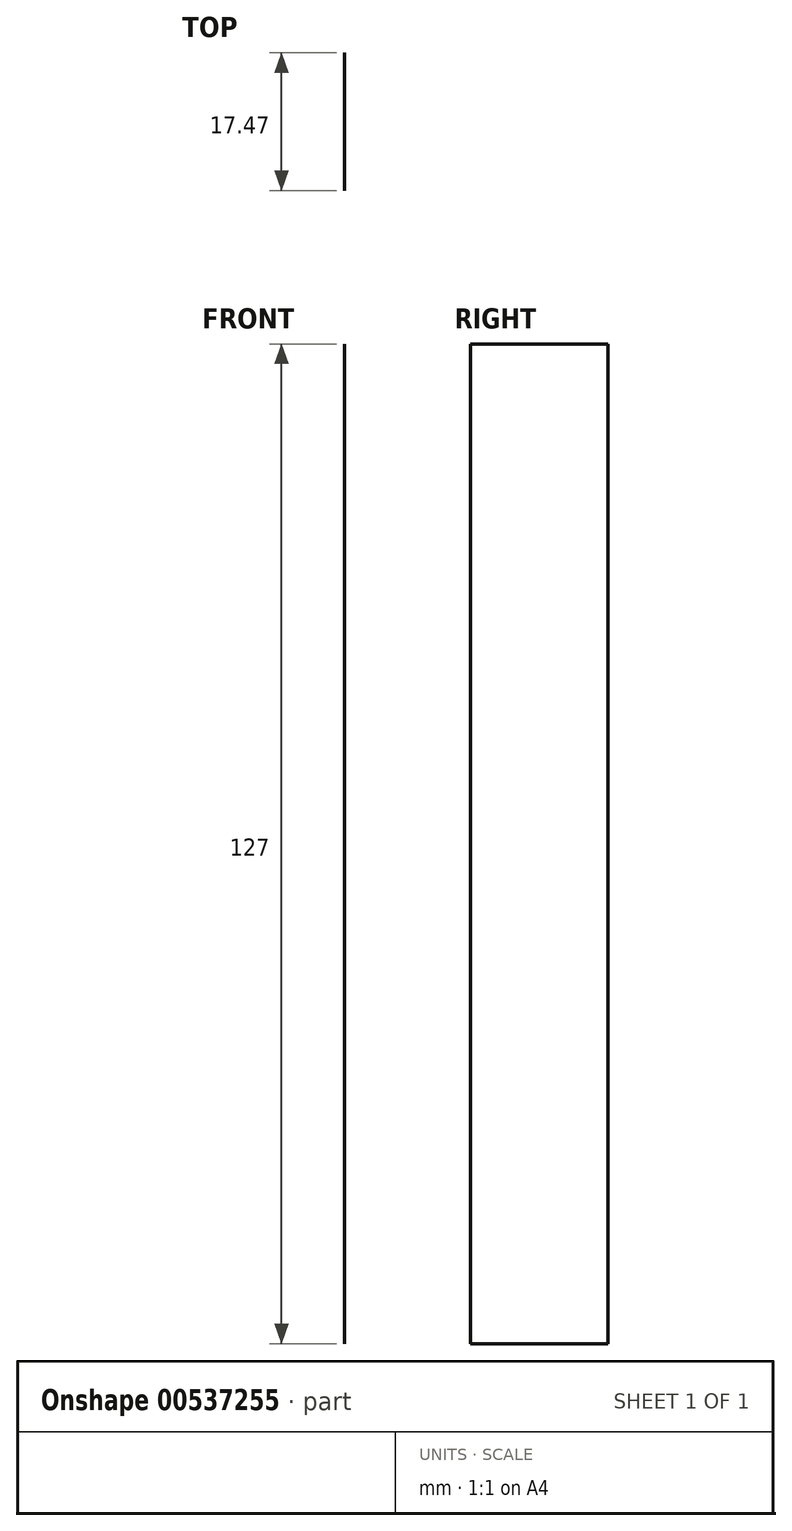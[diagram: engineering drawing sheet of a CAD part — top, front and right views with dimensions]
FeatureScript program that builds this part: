
annotation { "Feature Type Name" : "Feature", "Feature Type Description" : "" }
export const myFeature = defineFeature(function(context is Context, id is Id, definition is map)
    precondition{}
    {
        {
            var Q0;
            Q0=qCreatedBy(makeId("Top.planeOp"),FACE);
            var sketch = newSketch(context, id + "F0", { "sketchPlane" : qUnion([Q0])});
            skLineSegment(sketch, "E0.bottom", {"start": v(-41.28, 9.52) * mm, "end": v(41.27, 9.53) * mm});
            skLineSegment(sketch, "E0.top", {"start": v(-41.28, -9.53) * mm, "end": v(41.28, -9.53) * mm});
            skLineSegment(sketch, "E0.left", {"start": v(-41.28, 9.52) * mm, "end": v(-41.28, -9.53) * mm});
            skLineSegment(sketch, "E0.right", {"start": v(41.27, 9.53) * mm, "end": v(41.28, -9.52) * mm});
            skPoint(sketch, "E0.middle", {"position": v(0, 0) * mm});
            skLineSegment(sketch, "E1.bottom", {"start": v(111.12, 38.1) * mm, "end": v(60.32, 38.1) * mm});
            skLineSegment(sketch, "E1.top", {"start": v(111.12, 66.68) * mm, "end": v(60.32, 66.68) * mm});
            skLineSegment(sketch, "E1.left", {"start": v(111.12, 38.1) * mm, "end": v(111.12, 66.68) * mm});
            skLineSegment(sketch, "E1.right", {"start": v(60.32, 38.1) * mm, "end": v(60.32, 66.68) * mm});
            skPoint(sketch, "E1.middle", {"position": v(85.72, 52.39) * mm});
            skLineSegment(sketch, "E2", {"start": v(41.27, 9.53) * mm, "end": v(41.27, 27) * mm});
            skArc(sketch, "E3", {"start": v(41.27, 27) * mm, "mid": v(45.92, 38.23) * mm, "end": v(57.15, 42.88) * mm});
            skLineSegment(sketch, "E4", {"start": v(57.15, 42.88) * mm, "end": v(98.59, 42.88) * mm});
            skLineSegment(sketch, "E5.0", {"start": v(57.15, 61.93) * mm, "end": v(98.59, 61.93) * mm});
            skArc(sketch, "E5.1", {"start": v(22.22, 27) * mm, "mid": v(32.45, 51.7) * mm, "end": v(57.15, 61.93) * mm});
            skLineSegment(sketch, "E5.2", {"start": v(22.22, 9.53) * mm, "end": v(22.22, 27) * mm});
            skLineSegment(sketch, "E6", {"start": v(98.59, 61.93) * mm, "end": v(98.59, 42.88) * mm});
            skLineSegment(sketch, "E7", {"start": v(98.59, 61.93) * mm, "end": v(98.59, 66.68) * mm});
            skLineSegment(sketch, "E8", {"start": v(98.59, 66.68) * mm, "end": v(98.59, 42.88) * mm});
            skLineSegment(sketch, "E9", {"start": v(98.59, 42.88) * mm, "end": v(98.59, 38.1) * mm});
            skFitSpline(sketch, "E10", {"points": [v(-41.28, 9.52) * mm, v(57.15, 61.93) * mm], "startDerivative": vector(1.02, 104.4) * mm, "endDerivative": vector(159.77, -28.93) * mm});
            skSolve(sketch);
        }
        {
            var Q0;
            Q0=makeQuery(id+"F0.imprint","IMPRINT",FACE,{"disambiguationData":[TD([[makeQuery(id+"F0.imprint","IMPRINT",EDGE,{"derivedFrom":sQuery(id+"F0.wireOp",EDGE,"E5.1")}),1.0]])]});
            var Q1;
            {var subQ3=sQuery(id+"F0.wireOp",EDGE,"E9");Q1=makeQuery(id+"F0.imprint","IMPRINT",FACE,{"disambiguationData":[TD([[makeQuery(id+"F0.imprint","IMPRINT",EDGE,{"derivedFrom":subQ3}),-1.0]])]});}
            var Q2;
            {var subQ0=sQuery(id+"F0.wireOp",EDGE,"E4");var subQ1=sQuery(id+"F0.wireOp",EDGE,"E1.right");var subQ2=makeQuery(id+"F0.imprint","INTERSECT",VERTEX,{"derivedFrom":[subQ1,subQ0]});Q2=makeQuery(id+"F0.imprint","IMPRINT",FACE,{"disambiguationData":[TD([[makeQuery(id+"F0.imprint","IMPRINT",EDGE,{"disambiguationData":[TD([[subQ2,-1.0]])],"derivedFrom":subQ1}),-1.0]])]});}
            var Q3;
            Q3=sQuery(id+"F0.wireOp",EDGE,"E5.2");
            extrude(context, id + "F1", {"entities" : qUnion([Q0, Q1, Q2]), "bodyType" : ToolBodyType.SURFACE, "operationType" : NewBodyOperationType.ADD, "surfaceEntities" : qUnion([Q3]), "endBound" : BoundingType.SYMMETRIC, "depth" : 127 * mm, "offsetDistance" : 25.4 * mm});
        }
    });
